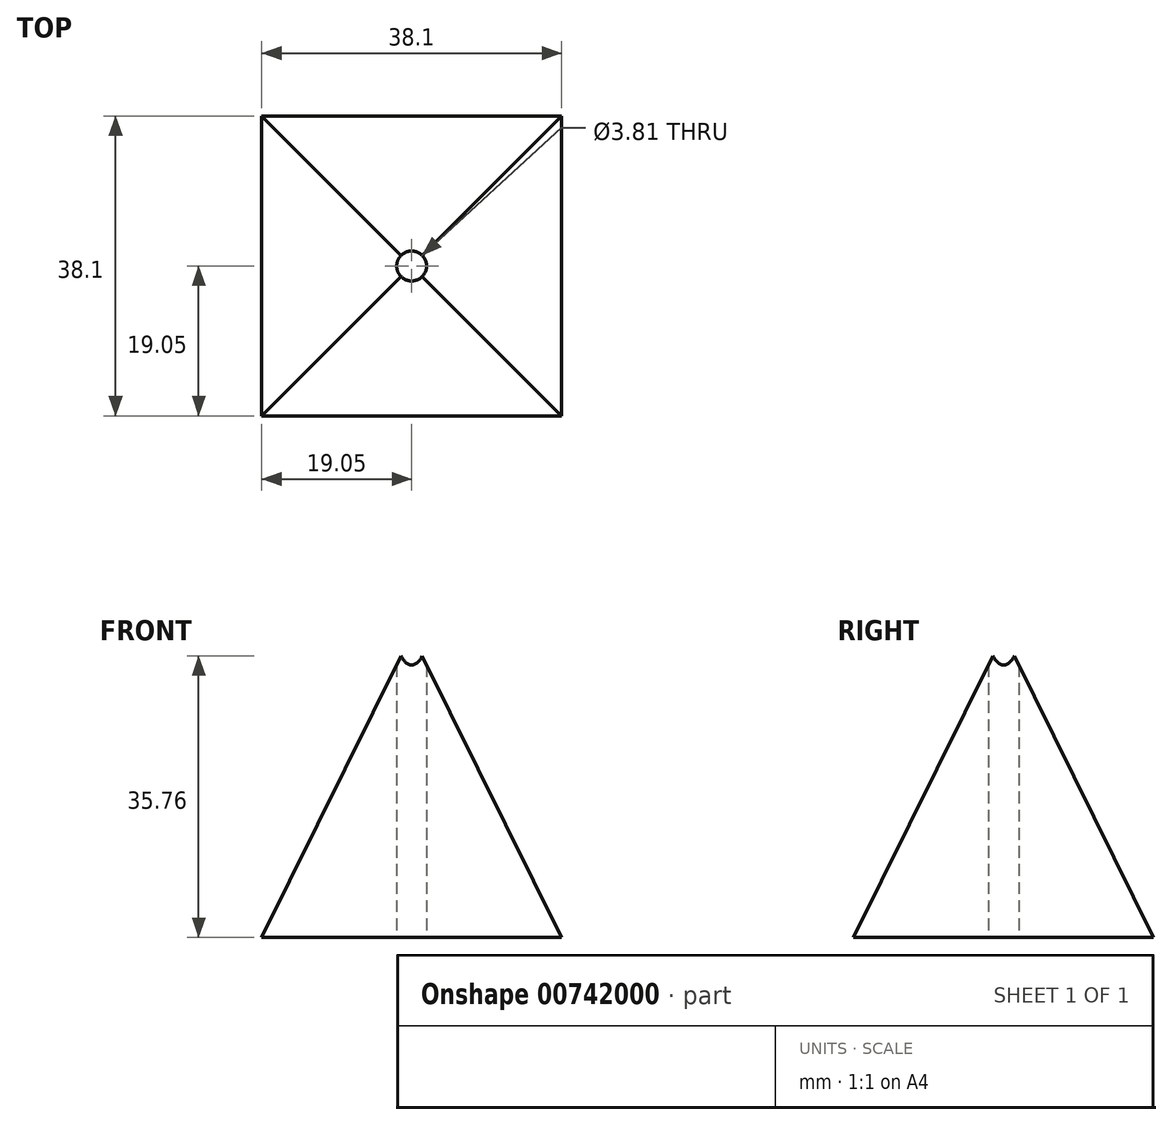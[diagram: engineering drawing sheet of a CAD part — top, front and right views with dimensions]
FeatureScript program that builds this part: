
annotation { "Feature Type Name" : "Feature", "Feature Type Description" : "" }
export const myFeature = defineFeature(function(context is Context, id is Id, definition is map)
    precondition{}
    {
        {
            var Q0;
            Q0=qCreatedBy(makeId("Top.planeOp"),FACE);
            var sketch = newSketch(context, id + "F0", { "sketchPlane" : qUnion([Q0])});
            skLineSegment(sketch, "E0.bottom", {"start": v(38.1, -38.1) * mm, "end": v(-38.1, -38.1) * mm});
            skLineSegment(sketch, "E0.top", {"start": v(38.1, 38.1) * mm, "end": v(-38.1, 38.1) * mm});
            skLineSegment(sketch, "E0.left", {"start": v(38.1, -38.1) * mm, "end": v(38.1, 38.1) * mm});
            skLineSegment(sketch, "E0.right", {"start": v(-38.1, -38.1) * mm, "end": v(-38.1, 38.1) * mm});
            skPoint(sketch, "E0.middle", {"position": v(0, 0) * mm});
            skSolve(sketch);
        }
        {
            var Q0;
            Q0=qCreatedBy(makeId("Top.planeOp"),FACE);
            cPlane(context, id + "F1", {"entities" : qUnion([Q0]), "cplaneType" : CPlaneType.OFFSET, "offset" : 38.1 * mm, "width" : 152.4 * mm, "height" : 152.4 * mm});
        }
        {
            var Q0;
            Q0=qCreatedBy(id+"F1.planeOp",FACE);
            var sketch = newSketch(context, id + "F2", { "sketchPlane" : qUnion([Q0])});
            skLineSegment(sketch, "E1.bottom", {"start": v(-19.05, 19.05) * mm, "end": v(19.05, 19.05) * mm});
            skLineSegment(sketch, "E1.top", {"start": v(-19.05, -19.05) * mm, "end": v(19.05, -19.05) * mm});
            skLineSegment(sketch, "E1.left", {"start": v(-19.05, 19.05) * mm, "end": v(-19.05, -19.05) * mm});
            skLineSegment(sketch, "E1.right", {"start": v(19.05, 19.05) * mm, "end": v(19.05, -19.05) * mm});
            skPoint(sketch, "E1.middle", {"position": v(0, 0) * mm});
            skSolve(sketch);
        }
        {
            var Q0;
            Q0=makeQuery(id+"F0.imprint","IMPRINT",FACE,{"disambiguationData":[TD([[makeQuery(id+"F0.imprint","IMPRINT",EDGE,{"derivedFrom":sQuery(id+"F0.wireOp",EDGE,"E0.bottom")}),-1.0]])]});
            var Q1;
            Q1=makeQuery(id+"F2.imprint","IMPRINT",FACE,{"disambiguationData":[TD([[makeQuery(id+"F2.imprint","IMPRINT",EDGE,{"derivedFrom":sQuery(id+"F2.wireOp",EDGE,"E1.bottom")}),-1.0]])]});
            var Q2;
            Q2=sQuery(id+"F2.wireOp",VERTEX,"E1.left.end");
            var Q3;
            Q3=sQuery(id+"F0.wireOp",VERTEX,"E0.right.start");
            var Q4;
            Q4=sQuery(id+"F2.wireOp",VERTEX,"E1.left.start");
            var Q5;
            Q5=sQuery(id+"F0.wireOp",VERTEX,"E0.right.end");
            var Q6;
            Q6=sQuery(id+"F2.wireOp",VERTEX,"E1.right.start");
            var Q7;
            Q7=sQuery(id+"F0.wireOp",VERTEX,"E0.left.end");
            var Q8;
            Q8=sQuery(id+"F2.wireOp",VERTEX,"E1.top.end");
            var Q9;
            Q9=sQuery(id+"F0.wireOp",VERTEX,"E0.left.start");
            loft(context, id + "F3", {"sheetProfilesArray" : [{ "sheetProfileEntities" : qUnion([Q0]) }, { "sheetProfileEntities" : qUnion([Q1]) }], "connections" : [{ "connectionEntities" : qUnion([Q2, Q3, Q4, Q5, Q6, Q7, Q8, Q9]), "connectionEdgeQueries" : qUnion([]), "connectionEdgeParameters" : [] }]});
        }
        {
            var Q0;
            Q0=qCreatedBy(id+"F1.planeOp",FACE);
            var sketch = newSketch(context, id + "F4", { "sketchPlane" : qUnion([Q0])});
            skLineSegment(sketch, "E2.bottom", {"start": v(19.05, -19.05) * mm, "end": v(-19.05, -19.05) * mm});
            skLineSegment(sketch, "E2.top", {"start": v(19.05, 19.05) * mm, "end": v(-19.05, 19.05) * mm});
            skLineSegment(sketch, "E2.left", {"start": v(19.05, -19.05) * mm, "end": v(19.05, 19.05) * mm});
            skLineSegment(sketch, "E2.right", {"start": v(-19.05, -19.05) * mm, "end": v(-19.05, 19.05) * mm});
            skPoint(sketch, "E2.middle", {"position": v(0, 0) * mm});
            skSolve(sketch);
        }
        {
            var Q0;
            Q0=qCreatedBy(makeId("Front.planeOp"),FACE);
            var sketch = newSketch(context, id + "F5", { "sketchPlane" : qUnion([Q0])});
            skLineSegment(sketch, "E3", {"start": v(0, 38.48) * mm, "end": v(0, 76.58) * mm});
            skSolve(sketch);
        }
        {
            var Q0;
            Q0=makeQuery(id+"F4.imprint","IMPRINT",FACE,{"disambiguationData":[TD([[makeQuery(id+"F4.imprint","IMPRINT",EDGE,{"derivedFrom":sQuery(id+"F4.wireOp",EDGE,"E2.bottom")}),-1.0]])]});
            var Q1;
            Q1=sQuery(id+"F5.wireOp",VERTEX,"E3.end");
            loft(context, id + "F6", {"sheetProfilesArray" : [{ "sheetProfileEntities" : qUnion([Q0]) }, { "sheetProfileEntities" : qUnion([Q1]) }]});
        }
        {
            var Q0;
            Q0=qCreatedBy(id+"F1.planeOp",FACE);
            var sketch = newSketch(context, id + "F7", { "sketchPlane" : qUnion([Q0])});
            skPoint(sketch, "E4", {"position": v(0, 0) * mm});
            skSolve(sketch);
        }
        {
            var Q0;
            Q0=sQuery(id+"F7.wireOp",VERTEX,"E4");
            var Q1;
            Q1=makeQuery(id+"F6.opLoft","SWEPT_BODY",BODY,{"disambiguationData":[OSD([makeQuery(id+"F4.imprint","IMPRINT",FACE,{"disambiguationData":[TD([[makeQuery(id+"F4.imprint","IMPRINT",EDGE,{"derivedFrom":sQuery(id+"F4.wireOp",EDGE,"E2.bottom")}),-1.0]])]}),sQuery(id+"F5.wireOp",VERTEX,"E3.end")])]});
            hole(context, id + "F8", {"style" : HoleStyle.SIMPLE, "endStyle" : HoleEndStyle.THROUGH, "oppositeDirection" : true, "holeDiameter" : 3.8 * mm, "majorDiameter" : 6.35 * mm, "isTappedThrough" : true, "tappedDepth" : 12.7 * mm, "tapClearance" : 3, "locations" : qUnion([Q0]), "scope" : qUnion([Q1])});
        }
        {
            var Q0;
            Q0=makeQuery(id+"F3.opLoft","CAP_FACE",FACE,{"disambiguationData":[OSD([makeQuery(id+"F2.imprint","IMPRINT",FACE,{"disambiguationData":[TD([[makeQuery(id+"F2.imprint","IMPRINT",EDGE,{"derivedFrom":sQuery(id+"F2.wireOp",EDGE,"E1.bottom")}),-1.0]])]})])],"isStart":true});
            var sketch = newSketch(context, id + "F9", { "sketchPlane" : qUnion([Q0])});
            skPoint(sketch, "E5", {"position": v(0, 0) * mm});
            skSolve(sketch);
        }
        {
            var Q0;
            Q0=sQuery(id+"F9.wireOp",VERTEX,"E5");
            var Q1;
            Q1=makeQuery(id+"F3.opLoft","SWEPT_BODY",BODY,{"disambiguationData":[OSD([makeQuery(id+"F0.imprint","IMPRINT",FACE,{"disambiguationData":[TD([[makeQuery(id+"F0.imprint","IMPRINT",EDGE,{"derivedFrom":sQuery(id+"F0.wireOp",EDGE,"E0.bottom")}),-1.0]])]}),makeQuery(id+"F2.imprint","IMPRINT",FACE,{"disambiguationData":[TD([[makeQuery(id+"F2.imprint","IMPRINT",EDGE,{"derivedFrom":sQuery(id+"F2.wireOp",EDGE,"E1.bottom")}),-1.0]])]})])]});
            hole(context, id + "F10", {"style" : HoleStyle.SIMPLE, "endStyle" : HoleEndStyle.THROUGH, "holeDiameter" : 3.8 * mm, "majorDiameter" : 6.35 * mm, "isTappedThrough" : true, "tappedDepth" : 12.7 * mm, "tapClearance" : 3, "locations" : qUnion([Q0]), "scope" : qUnion([Q1])});
        }
        {
            var Q0;
            Q0=makeQuery(id+"F3.opLoft","SWEPT_BODY",BODY,{"disambiguationData":[OSD([makeQuery(id+"F0.imprint","IMPRINT",FACE,{"disambiguationData":[TD([[makeQuery(id+"F0.imprint","IMPRINT",EDGE,{"derivedFrom":sQuery(id+"F0.wireOp",EDGE,"E0.bottom")}),-1.0]])]}),makeQuery(id+"F2.imprint","IMPRINT",FACE,{"disambiguationData":[TD([[makeQuery(id+"F2.imprint","IMPRINT",EDGE,{"derivedFrom":sQuery(id+"F2.wireOp",EDGE,"E1.bottom")}),-1.0]])]})])]});
            deleteBodies(context, id + "F11", {"entities" : qUnion([Q0])});
        }
    });
